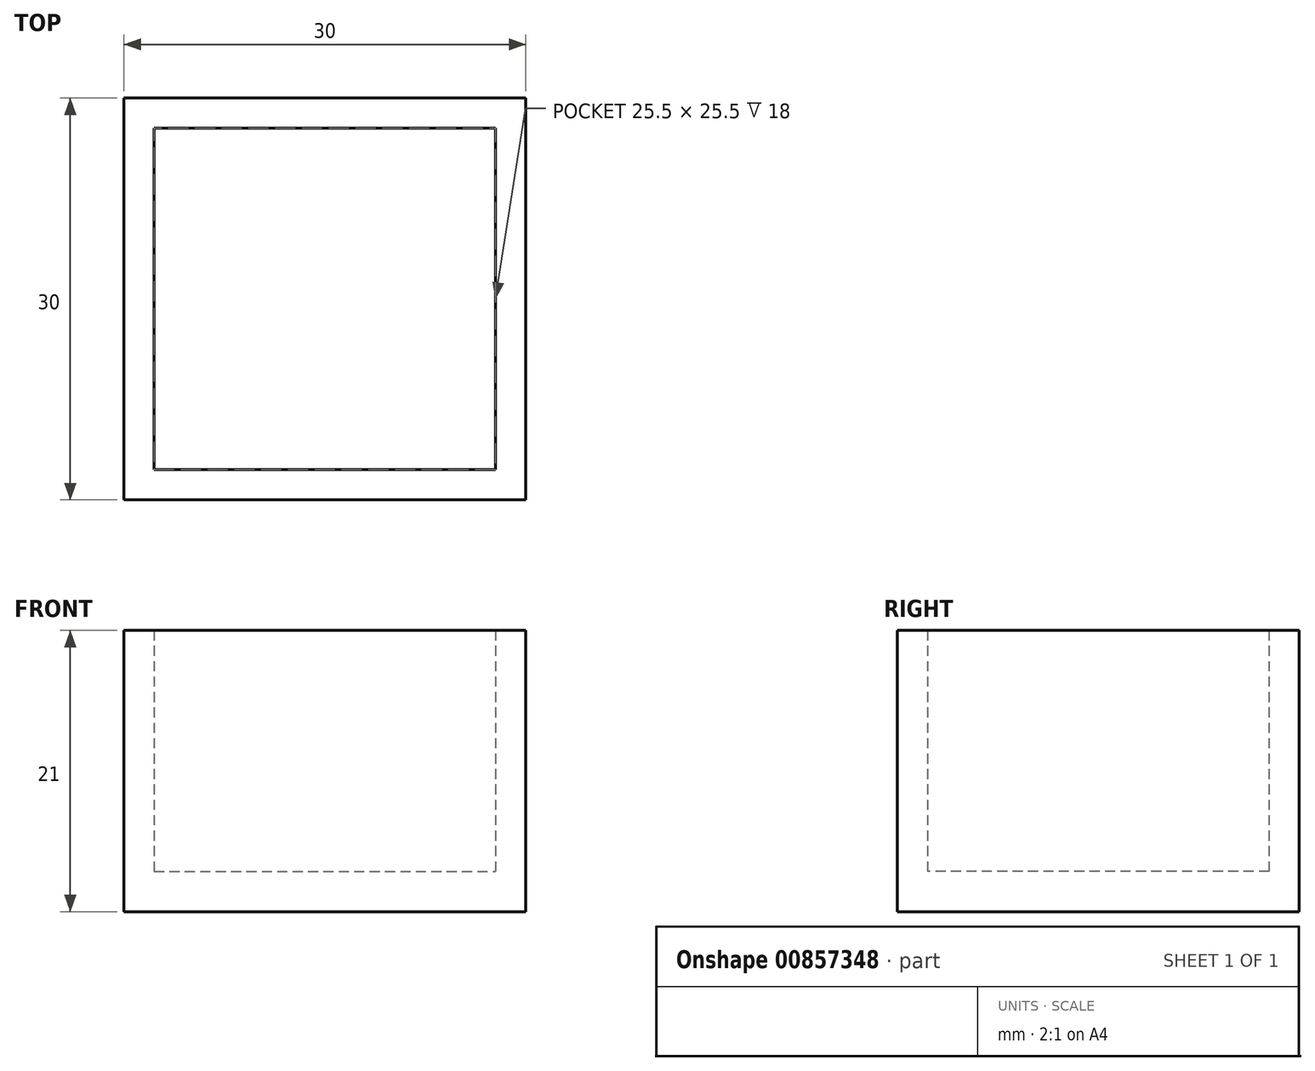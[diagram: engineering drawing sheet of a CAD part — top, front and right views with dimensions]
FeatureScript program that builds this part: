
annotation { "Feature Type Name" : "Feature", "Feature Type Description" : "" }
export const myFeature = defineFeature(function(context is Context, id is Id, definition is map)
    precondition{}
    {
        {
            var Q0;
            Q0=qCreatedBy(makeId("Top.planeOp"),FACE);
            var sketch = newSketch(context, id + "F0", { "sketchPlane" : qUnion([Q0])});
            skLineSegment(sketch, "E0.bottom", {"start": v(-15, 15) * mm, "end": v(15, 15) * mm});
            skLineSegment(sketch, "E0.top", {"start": v(-15, -15) * mm, "end": v(15, -15) * mm});
            skLineSegment(sketch, "E0.left", {"start": v(-15, 15) * mm, "end": v(-15, -15) * mm});
            skLineSegment(sketch, "E0.right", {"start": v(15, 15) * mm, "end": v(15, -15) * mm});
            skPoint(sketch, "E0.middle", {"position": v(0, 0) * mm});
            skSolve(sketch);
        }
        {
            var Q0;
            Q0=makeQuery(id+"F0.imprint","IMPRINT",FACE,{"disambiguationData":[TD([[makeQuery(id+"F0.imprint","IMPRINT",EDGE,{"derivedFrom":sQuery(id+"F0.wireOp",EDGE,"E0.bottom")}),-1.0]])]});
            extrude(context, id + "F1", {"entities" : qUnion([Q0]), "depth" : 3 * mm, "offsetDistance" : 25 * mm});
        }
        {
            var Q0;
            Q0=makeQuery(id+"F1.opExtrude","CAP_FACE",FACE,{"disambiguationData":[OSD([sQuery(id+"F0.wireOp",EDGE,"E0.bottom"),sQuery(id+"F0.wireOp",EDGE,"E0.top"),sQuery(id+"F0.wireOp",EDGE,"E0.left"),sQuery(id+"F0.wireOp",EDGE,"E0.right")])],"isStart":false});
            var sketch = newSketch(context, id + "F2", { "sketchPlane" : qUnion([Q0])});
            skLineSegment(sketch, "E1.bottom", {"start": v(-15, 15) * mm, "end": v(15, 15) * mm});
            skLineSegment(sketch, "E1.top", {"start": v(-15, -15) * mm, "end": v(15, -15) * mm});
            skLineSegment(sketch, "E1.left", {"start": v(-15, 15) * mm, "end": v(-15, -15) * mm});
            skLineSegment(sketch, "E1.right", {"start": v(15, 15) * mm, "end": v(15, -15) * mm});
            skPoint(sketch, "E1.middle", {"position": v(0, 0) * mm});
            skLineSegment(sketch, "E2.0", {"start": v(-12.75, 12.75) * mm, "end": v(12.75, 12.75) * mm});
            skLineSegment(sketch, "E2.1", {"start": v(-12.75, 12.75) * mm, "end": v(-12.75, -12.75) * mm});
            skLineSegment(sketch, "E2.2", {"start": v(-12.75, -12.75) * mm, "end": v(12.75, -12.75) * mm});
            skLineSegment(sketch, "E2.3", {"start": v(12.75, 12.75) * mm, "end": v(12.75, -12.75) * mm});
            skSolve(sketch);
        }
        {
            var Q0;
            Q0 = qSketchRegion(id + "F2", true);
            extrude(context, id + "F3", {"entities" : qUnion([Q0]), "operationType" : NewBodyOperationType.ADD, "depth" : 18 * mm, "offsetDistance" : 25 * mm});
        }
    });
